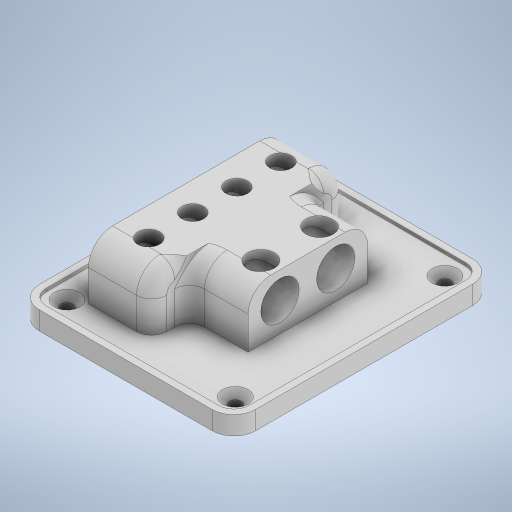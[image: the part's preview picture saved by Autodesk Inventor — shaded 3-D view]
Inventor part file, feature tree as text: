
AUTODESK INVENTOR PART (.ipt)
format: ipt  version: 2023 (Build 270158000, 158)  size: 574,464 bytes
history: native  units: in
note: dims shown in document units (in); Inventor stores cm internally (conversion verified against a paired STEP export)
features: fillet x8, extrude x7, sketch x6, chamfer x1
ambient origin geometry x8: Origin, YZ Plane, XZ Plane, XY Plane, X Axis, Y Axis, Z Axis, Center Point
bodies: Solid1 (feature_tree)
feature tree (22):
  sketch  "Sketch1"  dims[d0=0.1969in d1=2.6575in]
  extrude  "Extrusion1"  Depth=0.1969in
  extrude  "Extrusion2"  Depth=1.6191in
  extrude  "Extrusion3"  Depth=0.2028in
  fillet  "Fillet1"  Radius=0.2028in
  fillet  "Fillet2"  Radius=0.2421in
  fillet  "Fillet3"  Radius=2.5591in
  fillet  "Fillet4"  Radius=1.5945in
  fillet  "Fillet5"  Radius=0.8268in
  fillet  "Fillet6"  Radius=0.8268in
  fillet  "Fillet7"  Radius=1.2795in
  fillet  "Fillet8"  Radius=1.565in
  extrude  "Extrusion4"  Depth=0.502in
  extrude  "Extrusion5"  Depth=0.315in
  extrude  "Extrusion6"  Depth=0.1969in
  extrude  "Extrusion7"  Depth=0.1969in
  chamfer  "Chamfer1"  Distance=0.1969in
  sketch  "Sketch2"  dims[d2=3.2382in d3=1.6191in]
  sketch  "Sketch3"  dims[d4=1.3287in d5=0.0886in d6=0.2028in d7=0.0in d8=0.2421in d9=0.0in d10=2.5591in d11=1.5945in d12=0.8268in d13=0.8268in d14=1.2795in d15=1.565in]
  sketch  "Sketch4"  dims[d16=0.7825in d17=0.502in]
  sketch  "Sketch5"  dims[d18=0.7268in d19=0.0in d20=0.315in]
  sketch  "Sketch6"  dims[d21=0.315in d22=0.1969in d23=0.1969in d24=0.1969in d25=0.1969in d26=0.2953in d27=0.2953in d28=0.502in d29=0.502in d30=0.7303in d31=0.3652in d32=0.3376in d33=0.689in d34=0.0in d35=0.4291in d37=0.5768in d38=0.5768in d39=0.5768in d40=0.3524in d43=0.2884in d44=0.5709in d45=0.0in d46=0.2864in d48=0.3543in d49=0.7677in d51=0.2303in d52=0.3839in d53=0.5768in d54=0.5768in d55=0.5768in d57=0.3755in d58=0.2884in d59=0.2756in d60=0.0in d61=0.1575in d62=0.1575in d63=0.1575in d64=0.1575in d65=0.2362in d66=0.3346in d67=0.3346in d68=0.315in d69=0.3346in d70=0.315in d71=0.3346in d72=0.315in d73=0.2756in d74=0.0in d75=0.0886in d76=0.0492in d77=45.0deg d78=0.315in]
